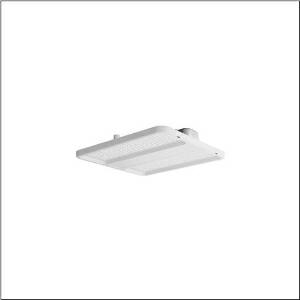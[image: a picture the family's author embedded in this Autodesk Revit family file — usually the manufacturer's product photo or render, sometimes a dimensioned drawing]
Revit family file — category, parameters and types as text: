
# Revit family: highbay_11_midi_51hn11da4fda
name_source: partatom
category: Lighting Fixtures
units: mm (PartAtom-declared; Revit-internal decimal feet)

## family parameters
Cut with Voids When Loaded = No
Host = Face
Light Source = No
Part Type = Normal
Room Calculation Point = No
Round Connector Dimension = Use Diameter
Shared = No

## types (1)
- --- (1 x LED, 2310 lm, 11.8 W, 4000K)
    Apparent Load = 12 VA
    CIE Flux Codes = 85 97 100 100 100
    Color Rendering = 80
    Color Temperature = 4000K
    Default Elevation = 1800 mm
    Description = high bay luminaire Highbay 11 midi; direct symmetric narrow distribution, light control with lens of PMMA; UGR ≤ 22 (X = 4H | Y = 8H | S = 0.25H | reflection values 70/50/20); luminous flux: 15.000lm; light colour: 840, colour temperature: 4000K, MacAdam ≤ 2 SDCM (initial), colour rendering: CRI > 80; luminous efficacy: 204,9lm/W; rated service life: 100.000h (L95/B50) at AT= 25°C; control: DALI 2; housing frame of high-performance plastic PA6, matt traffic white (RAL 9016); cover of PMMA; dimension (LxWxH): 474 x 442 x 72mm; luminaire connection: terminal, 5-pole, max. 2.5mm² (cable entry for one cable, Ø 8.5..16mm); mains connection: 230..240V, AC/DC 0/50..60Hz; connected load: 73,2W; protection rating (complete): IP66; insulation class (complete): insulation class I (protective earthing); protection symbol: D; impact resistance: IK08; halogen-free wiring; for central battery installations according to DIN EN 60598-2-22; corresponds to IFS (International Featured Standards) requirements for safety and quality in the food industry; LABS conformity tested according to VDMA 24364:2018-05; certification: CE, ENEC, VDE, UKCA; permissible operating ambient temperature: -40..+65°C (reducing of maximum allowable ambient temperature of 5°C with ceiling mounting); packaging unit: 1 piece; (delivery without accessories; please order mounting accessories separately)
    Height = 72 mm  [stored 0.23622 ft]
    Lamp = 1 x LED
    Lamp Light Flux = 2310 lm
    Lamp Power = 11.8 W
    Lamp count = 1
    Length = 474 mm
    Luminous efficacy = 196 lm/W
    Manufacturer = Siteco
    ModVariant = No
    Model = 51HN11DA4FDA
    Mounting Place = Ceiling
    Mounting Type = Pendant
    Number of Poles = 1
    OnlyDefault = Yes
    Power Factor = 1
    Product Name = Highbay 11 midi
    Product group = high bay luminaire
    ProductGroupID = 901
    Protection Class = Protection class I
    Protection Degree = IP 66
    RLX_Detail_Level = 1
    RLX_Emergency_Light_Flux = 0 lm
    RLX_Emergency_Type = 0
    RLX_Emergency_Type_DB = No
    RlxData = <blob elided: 16765 chars, md5=a46a4dae>
    Socket = socket
    Standby Power = 0 W
    System Light Flux = 2310 lm
    System Power = 12 W
    Type Comments = : DC mode (central or group accumulator) initial emergency light level
    Type Image = l_1363240.jpg
    URL = http://relux.com
    VarID = @adj_003727
    Voltage = 0 V
    Weight = 0.00 kg
    Width = 442 mm

note: [stored X ft] marks values corroborated as IEEE doubles in the binary element streams (Revit-internal decimal feet)

## geometry (parser evidence)
native form markers: Blend x4, Sweep x11
no freeform markers — native parametric forms only
